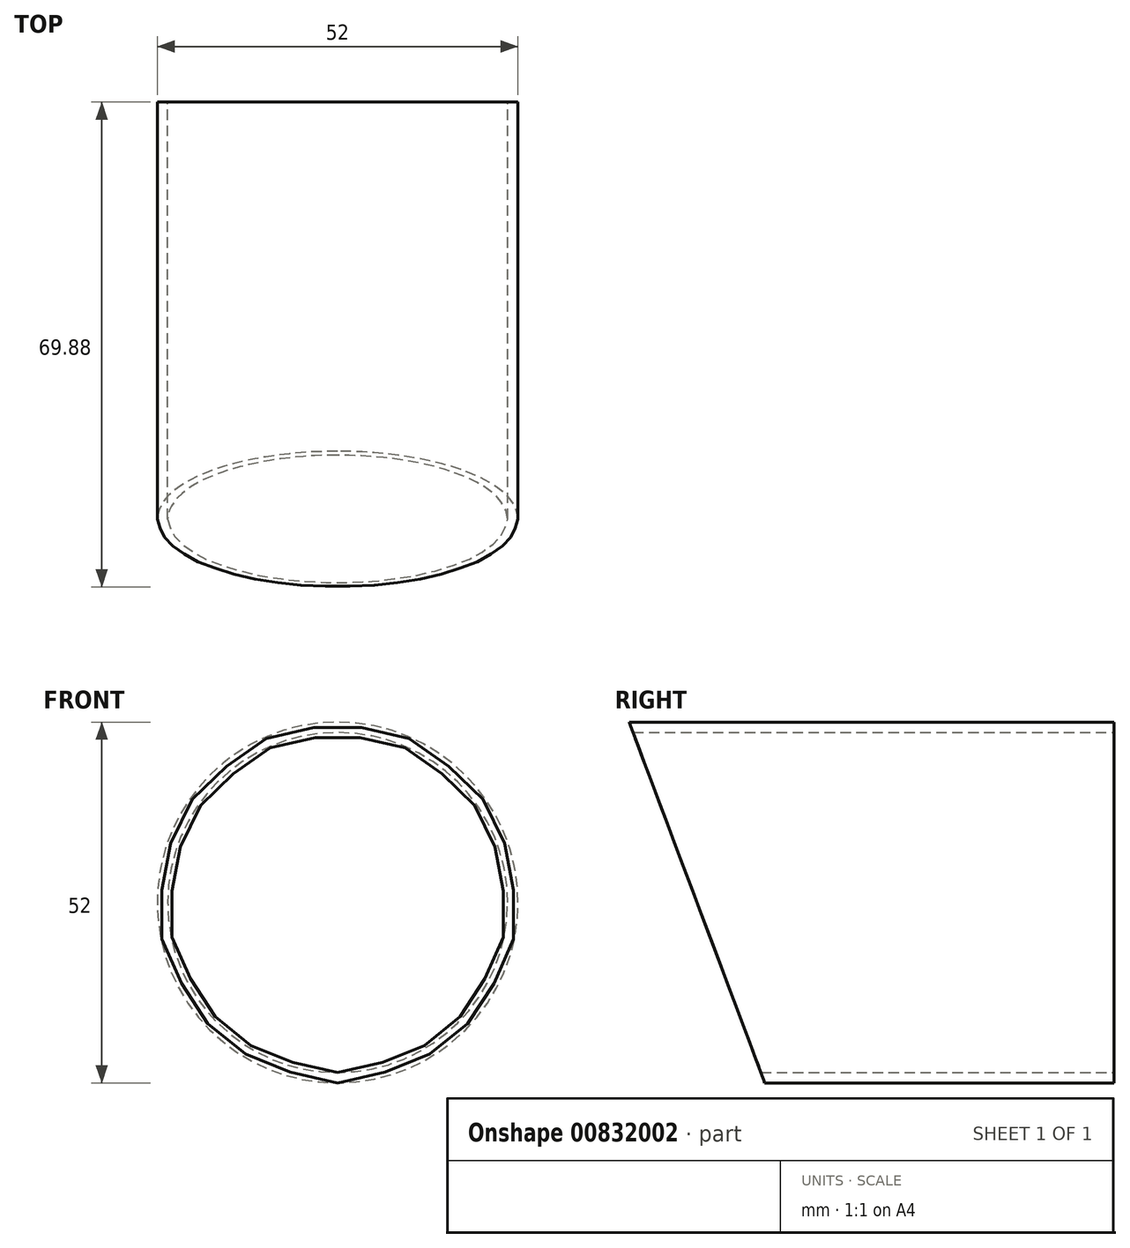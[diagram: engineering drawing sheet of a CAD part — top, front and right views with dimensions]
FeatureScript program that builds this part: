
annotation { "Feature Type Name" : "Feature", "Feature Type Description" : "" }
export const myFeature = defineFeature(function(context is Context, id is Id, definition is map)
    precondition{}
    {
        {
            var Q0;
            Q0=qCreatedBy(makeId("Front.planeOp"),FACE);
            var sketch = newSketch(context, id + "F0", { "sketchPlane" : qUnion([Q0])});
            skCircle(sketch, "E0", {"center": v(0, 0) * mm, "radius": 24.5 * mm});
            skCircle(sketch, "E1", {"center": v(0, 0) * mm, "radius": 26 * mm});
            skSolve(sketch);
        }
        {
            var Q0;
            Q0 = qSketchRegion(id + "F0", true);
            extrude(context, id + "F1", {"entities" : qUnion([Q0]), "depth" : 70 * mm, "offsetDistance" : 25 * mm});
        }
        {
            var Q0;
            Q0=qCreatedBy(makeId("Right.planeOp"),FACE);
            var sketch = newSketch(context, id + "F2", { "sketchPlane" : qUnion([Q0])});
            skLineSegment(sketch, "E2", {"start": v(-73.68, -28.4) * mm, "end": v(-49.42, -28.4) * mm});
            skLineSegment(sketch, "E3", {"start": v(-49.42, -28.4) * mm, "end": v(-70.48, 27.6) * mm});
            skLineSegment(sketch, "E4", {"start": v(-70.48, 27.6) * mm, "end": v(-73.68, -28.4) * mm});
            skSolve(sketch);
        }
        {
            var Q0;
            Q0 = qSketchRegion(id + "F2", true);
            extrude(context, id + "F3", {"entities" : qUnion([Q0]), "operationType" : NewBodyOperationType.REMOVE, "oppositeDirection" : true, "depth" : 30 * mm, "offsetDistance" : 25 * mm, "hasSecondDirection" : true, "secondDirectionOppositeDirection" : false, "secondDirectionDepth" : 30 * mm});
        }
    });
